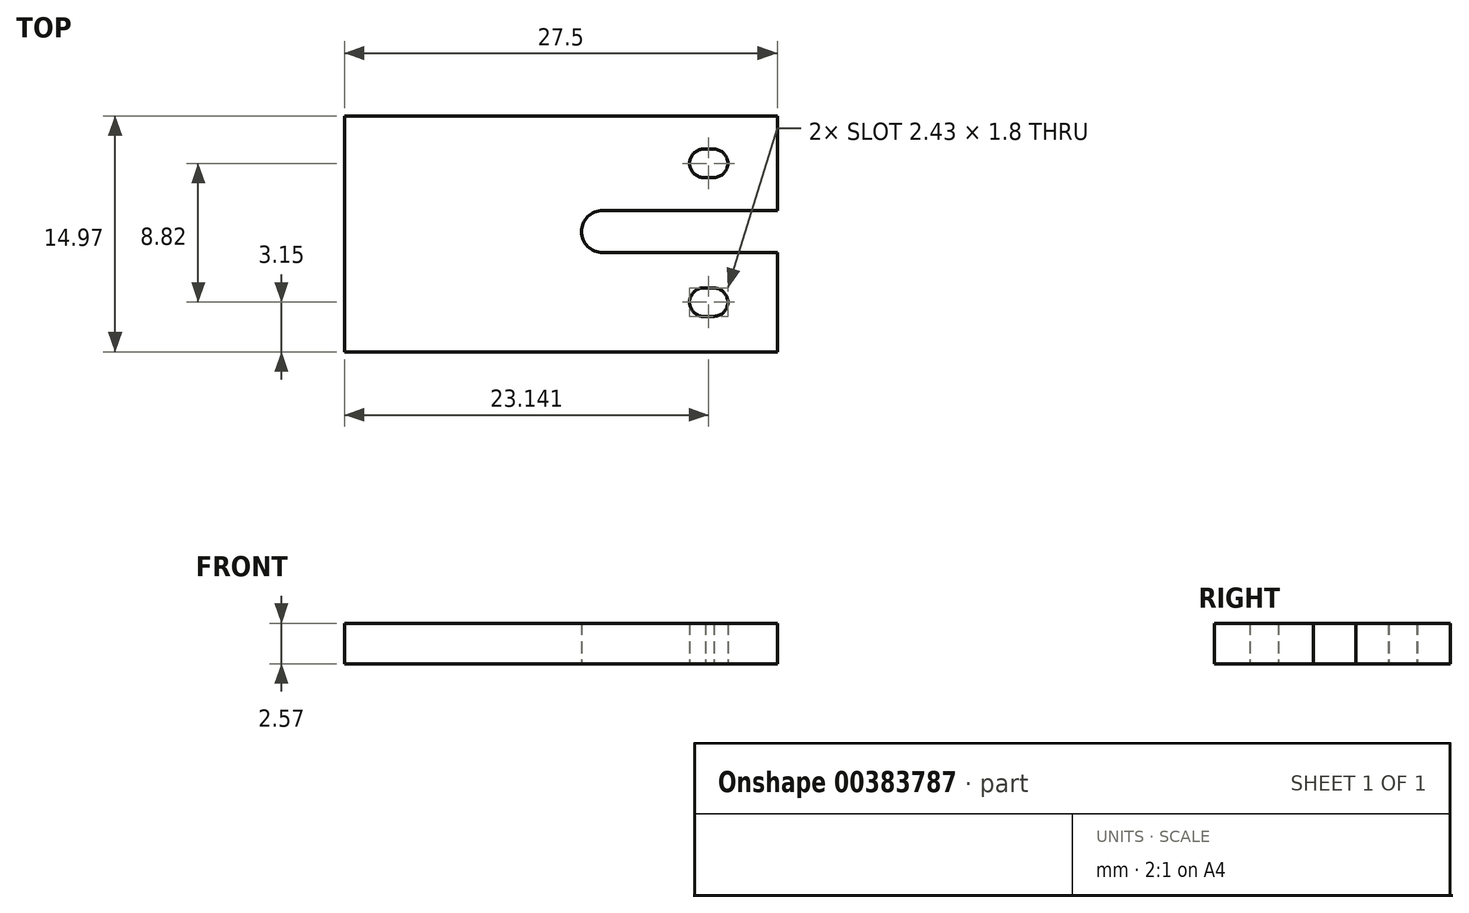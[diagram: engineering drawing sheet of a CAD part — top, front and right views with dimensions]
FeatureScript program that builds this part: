
annotation { "Feature Type Name" : "Feature", "Feature Type Description" : "" }
export const myFeature = defineFeature(function(context is Context, id is Id, definition is map)
    precondition{}
    {
        {
            var Q0;
            Q0=qCreatedBy(makeId("Top.planeOp"),FACE);
            var sketch = newSketch(context, id + "F0", { "sketchPlane" : qUnion([Q0])});
            skLineSegment(sketch, "E0.bottom", {"start": v(-16.88, 14.97) * mm, "end": v(10.62, 14.97) * mm});
            skLineSegment(sketch, "E0.top", {"start": v(-16.88, 0) * mm, "end": v(10.62, 0) * mm});
            skLineSegment(sketch, "E0.left", {"start": v(-16.88, 14.97) * mm, "end": v(-16.88, 0) * mm});
            skLineSegment(sketch, "E0.right", {"start": v(10.62, 14.97) * mm, "end": v(10.62, 8.97) * mm});
            skLineSegment(sketch, "E1", {"start": v(10.62, 14.97) * mm, "end": v(16.76, 14.97) * mm, "construction": true});
            skLineSegment(sketch, "E2", {"start": v(16.76, 14.97) * mm, "end": v(16.76, 8.97) * mm, "construction": true});
            skLineSegment(sketch, "E3", {"start": v(10.62, 0) * mm, "end": v(16.92, 0) * mm, "construction": true});
            skLineSegment(sketch, "E4", {"start": v(16.92, 0) * mm, "end": v(16.92, 6.3) * mm, "construction": true});
            skLineSegment(sketch, "E5", {"start": v(-16.88, 14.97) * mm, "end": v(-16.88, 20.8) * mm, "construction": true});
            skLineSegment(sketch, "E6", {"start": v(-0.48, 8.97) * mm, "end": v(-0.48, 6.3) * mm, "construction": true});
            skArc(sketch, "E7", {"start": v(-0.48, 6.3) * mm, "mid": v(-1.81, 7.63) * mm, "end": v(-0.48, 8.97) * mm});
            skLineSegment(sketch, "E8", {"start": v(-0.48, 8.97) * mm, "end": v(10.62, 8.97) * mm});
            skLineSegment(sketch, "E9", {"start": v(-0.48, 6.3) * mm, "end": v(10.62, 6.3) * mm});
            skLineSegment(sketch, "E10", {"start": v(10.62, 14.97) * mm, "end": v(10.62, 20.43) * mm, "construction": true});
            skLineSegment(sketch, "E11", {"start": v(10.62, 20.43) * mm, "end": v(7.47, 20.43) * mm, "construction": true});
            skLineSegment(sketch, "E12", {"start": v(7.47, 20.43) * mm, "end": v(7.47, 17.3) * mm, "construction": true});
            skLineSegment(sketch, "E13", {"start": v(7.47, 17.3) * mm, "end": v(5.05, 17.3) * mm, "construction": true});
            skLineSegment(sketch, "E14", {"start": v(16.76, 11.97) * mm, "end": v(1.72, 11.97) * mm, "construction": true});
            skCircle(sketch, "E15", {"center": v(16.76, 11.97) * mm, "radius": 0.9 * mm, "construction": true});
            skLineSegment(sketch, "E16", {"start": v(16.76, 12.87) * mm, "end": v(1.58, 12.87) * mm, "construction": true});
            skLineSegment(sketch, "E17", {"start": v(16.76, 11.07) * mm, "end": v(1.8, 11.07) * mm, "construction": true});
            skLineSegment(sketch, "E18", {"start": v(5.05, 17.3) * mm, "end": v(5.05, 11.07) * mm, "construction": true});
            skLineSegment(sketch, "E19", {"start": v(7.47, 17.3) * mm, "end": v(7.47, 11.07) * mm, "construction": true});
            skArc(sketch, "E20", {"start": v(6.07, 11.07) * mm, "mid": v(5.05, 11.97) * mm, "end": v(6.07, 12.87) * mm});
            skArc(sketch, "E21", {"start": v(6.6, 11.07) * mm, "mid": v(7.48, 11.97) * mm, "end": v(6.6, 12.87) * mm});
            skLineSegment(sketch, "E22", {"start": v(6.07, 12.87) * mm, "end": v(6.6, 12.87) * mm});
            skLineSegment(sketch, "E23", {"start": v(6.07, 11.07) * mm, "end": v(6.6, 11.07) * mm});
            skLineSegment(sketch, "E24.trimOffspring", {"start": v(10.62, 6.3) * mm, "end": v(10.62, 0) * mm});
            skLineSegment(sketch, "E25", {"start": v(16.92, 3.15) * mm, "end": v(-0.92, 3.15) * mm, "construction": true});
            skPoint(sketch, "E25.endSnap0", {"position": v(10.62, 3.15) * mm});
            skLineSegment(sketch, "E26", {"start": v(5.05, 11.85) * mm, "end": v(5.05, 3.15) * mm, "construction": true});
            skLineSegment(sketch, "E27", {"start": v(1.72, 11.97) * mm, "end": v(1.8, 3.15) * mm, "construction": true});
            skLineSegment(sketch, "E28", {"start": v(1.8, 3.15) * mm, "end": v(1.76, 7.56) * mm, "construction": true});
            skLineSegment(sketch, "E29", {"start": v(1.76, 7.56) * mm, "end": v(13.21, 7.56) * mm, "construction": true});
            skArc(sketch, "E30.MirrorCS", {"start": v(6.07, 4.05) * mm, "mid": v(5.05, 3.15) * mm, "end": v(6.07, 2.25) * mm});
            skArc(sketch, "E31.MirrorCS", {"start": v(6.6, 4.05) * mm, "mid": v(7.48, 3.15) * mm, "end": v(6.6, 2.25) * mm});
            skLineSegment(sketch, "E32", {"start": v(6.07, 4.05) * mm, "end": v(6.6, 4.05) * mm});
            skLineSegment(sketch, "E33", {"start": v(6.07, 2.25) * mm, "end": v(6.6, 2.25) * mm});
            skSolve(sketch);
        }
        {
            var Q0;
            Q0=makeQuery(id+"F0.imprint","IMPRINT",FACE,{"disambiguationData":[TD([[makeQuery(id+"F0.imprint","IMPRINT",EDGE,{"derivedFrom":sQuery(id+"F0.wireOp",EDGE,"E0.bottom")}),-1.0]])]});
            extrude(context, id + "F1", {"entities" : qUnion([Q0]), "depth" : 2.57 * mm});
        }
    });
